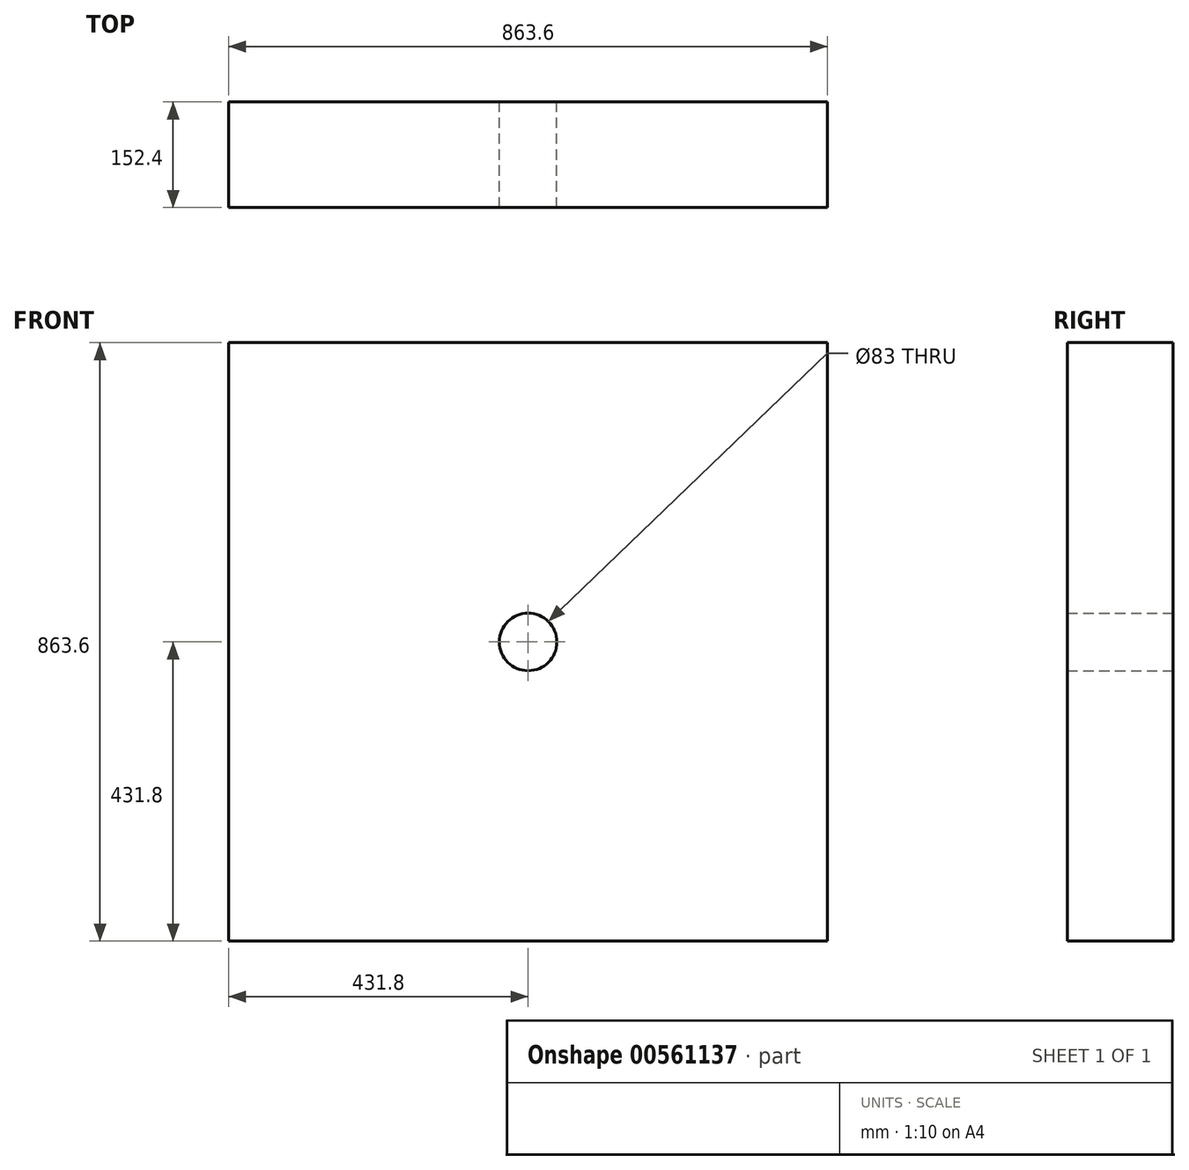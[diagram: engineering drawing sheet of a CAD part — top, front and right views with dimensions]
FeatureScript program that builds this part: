
annotation { "Feature Type Name" : "Feature", "Feature Type Description" : "" }
export const myFeature = defineFeature(function(context is Context, id is Id, definition is map)
    precondition{}
    {
        {
            var Q0;
            Q0=qCreatedBy(makeId("Front.planeOp"),FACE);
            var sketch = newSketch(context, id + "F0", { "sketchPlane" : qUnion([Q0])});
            skLineSegment(sketch, "E0.bottom", {"start": v(-431.8, 431.8) * mm, "end": v(431.8, 431.8) * mm});
            skLineSegment(sketch, "E0.top", {"start": v(-431.8, -431.8) * mm, "end": v(431.8, -431.8) * mm});
            skLineSegment(sketch, "E0.left", {"start": v(-431.8, 431.8) * mm, "end": v(-431.8, -431.8) * mm});
            skLineSegment(sketch, "E0.right", {"start": v(431.8, 431.8) * mm, "end": v(431.8, -431.8) * mm});
            skCircle(sketch, "E1", {"center": v(0, 0) * mm, "radius": 41.5 * mm});
            skSolve(sketch);
        }
        {
            var Q0;
            Q0 = qSketchRegion(id + "F0", true);
            extrude(context, id + "F1", {"entities" : qUnion([Q0]), "depth" : 152.4 * mm, "offsetDistance" : 25 * mm});
        }
    });
